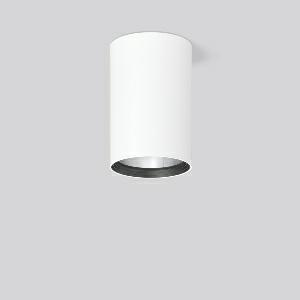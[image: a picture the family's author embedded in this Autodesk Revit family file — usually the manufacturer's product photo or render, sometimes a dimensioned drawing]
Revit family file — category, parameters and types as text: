
# Revit family: heledon_maxi_a_931225_002_2_76_fbd7
name_source: partatom
category: Lighting Fixtures
units: mm (PartAtom-declared; Revit-internal decimal feet)

## family parameters
Cut with Voids When Loaded = No
Host = Face
Light Source = No
Part Type = Normal
Room Calculation Point = No
Round Connector Dimension = Use Diameter
Shared = No

## types (1)
- HELEDON maxi A (1 x LED Modul 927, 4100 lm, 2700)
    Apparent Load = 35 VA
    Approval mark = CE
    CIE Flux Codes = 100 100 100 100 100
    Color Rendering = 92
    Color Temperature = 2700
    Default Elevation = 1800 mm
    Description = Series: HELEDON maxi
Cylindrical surface-mounted downlight. Housing: die-cast aluminium, powder-coated. Internal ceiling frame polycarbonate with bayonet mounting. Black plastic ring and recessed LED to prevent glare from the side. Optical assembly with reflector made of MIRO-Silver with 98% total light reflection for outstanding efficiency - can be changed without tools. Best colour rendering index Ra>90. Suitable for Ceiling mounting. Easy installation with a separate ceiling frame with bayonet mounting and plug connection. Driver integrated. Connected via plug-in connector. High quality converter without flickering and stroboscopic effect. The following accessories can be mounted without use of tools: interchangeable lenses, decorative glasses, honeycomb louvre, clear and frosted diffusers, white interchangeable plastic ring. 
Colour: traffic white, matt (RAL 9016)
Diameter: 123 mm
Height: 183 mm
Lamp: LED
Socket: without socket
Colour temperature: 2700K
Colour rendering index (CRI): 92
System power: 35 W
Rated luminous flux: 4100 lm
Luminous efficiency: 117 lm/W
Control gear: Converter, dimmable, DALI
Protection class: I
Type of protection: IP 20
    Height = 183 mm
    Lamp = 1 x LED Modul 927
    Lamp Light Flux = 4100 lm
    Lamp count = 1
    Length = 123 mm
    Lifetime = 50000 h
    Luminous efficacy = 117 lm/W
    Manufacturer = RZB
    ModVariant = No
    Model = 931225.002.2.76
    Mounting Place = Ceiling
    Mounting Type = Surface mounted
    Number of Poles = 1
    OnlyDefault = Yes
    Power Factor = 1
    Product Name = HELEDON maxi A
    Product group = Surface mounted downlights
    ProductGroupID = 302
    Protection Class = Protection class I
    Protection Degree = IP 20
    RLX_Detail_Level = 1
    RLX_Emergency_Light_Flux = 0 lm
    RLX_Emergency_Type = 0
    RLX_Emergency_Type_DB = No
    RlxData = <blob elided: 99437 chars, md5=284e71b0>
    Socket = socket
    Standby Power = 0 W
    System Light Flux = 4100 lm
    System Power = 35 W
    Type Comments = Product without accessories
    Type Image = 931192.002.jpg
    URL = http://relux.com
    VarID = ---
    Voltage = 230 V
    Voltage Range = 220-240 V
    Weight = 0.00 kg
    Width = 0 mm  [stored 0 ft]

note: [stored X ft] marks values corroborated as IEEE doubles in the binary element streams (Revit-internal decimal feet)

## geometry (parser evidence)
native form markers: Blend x4, Sweep x11
no freeform markers — native parametric forms only
